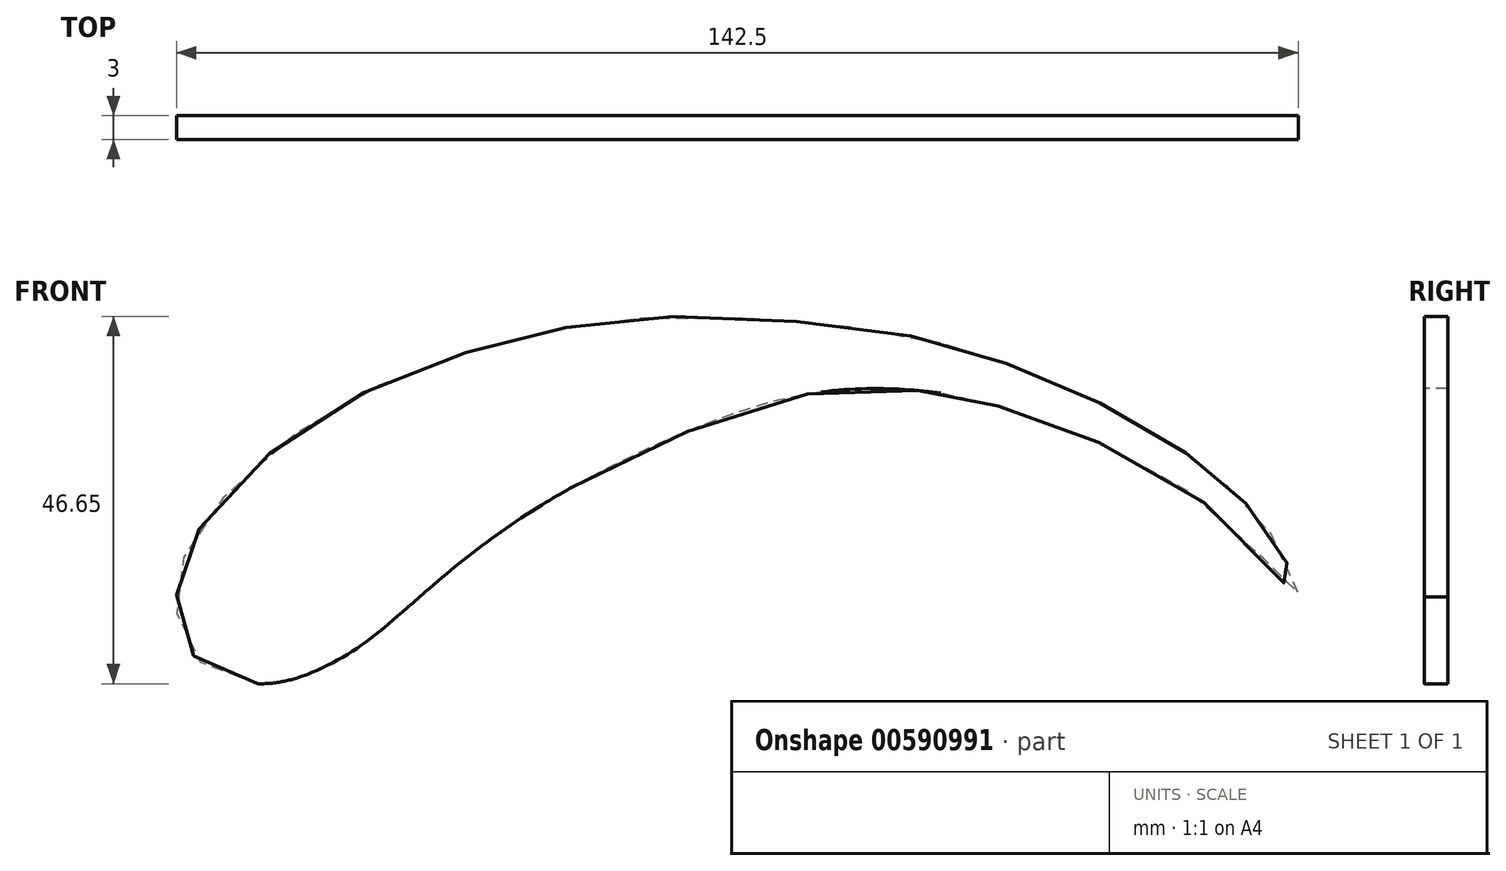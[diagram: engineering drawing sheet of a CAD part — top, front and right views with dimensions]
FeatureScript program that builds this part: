
annotation { "Feature Type Name" : "Feature", "Feature Type Description" : "" }
export const myFeature = defineFeature(function(context is Context, id is Id, definition is map)
    precondition{}
    {
        {
            var Q0;
            Q0=qCreatedBy(makeId("Front.planeOp"),FACE);
            var sketch = newSketch(context, id + "F0", { "sketchPlane" : qUnion([Q0])});
            skFitSpline(sketch, "E0", {"points": [v(70.77, 8.65) * mm, v(64.93, 15.14) * mm, v(49.3, 26.46) * mm, v(33.38, 32.65) * mm, v(25.04, 34.55) * mm, v(9.61, 34.55) * mm, v(-10.88, 27.85) * mm, v(-29.95, 17.24) * mm, v(-42.33, 7.26) * mm, v(-49.15, 1.83) * mm, v(-56.48, -1.7) * mm, v(-63.05, -2.21) * mm, v(-69.11, 0.76) * mm, v(-71.44, 5.7) * mm, v(-71.33, 11.53) * mm, v(-68.1, 18.3) * mm, v(-56.75, 29.26) * mm, v(-41.91, 37.2) * mm, v(-27.15, 41.76) * mm, v(-12.91, 44.04) * mm, v(7.32, 43.62) * mm, v(24.64, 41.1) * mm, v(36.92, 37.07) * mm, v(50.06, 30.99) * mm, v(59.9, 24.38) * mm, v(65.08, 19.5) * mm, v(69.06, 13.64) * mm, v(70.77, 8.65) * mm]});
            skFitSpline(sketch, "E1", {"points": [v(9.58, 31.44) * mm, v(18.14, 32.26) * mm, v(27.38, 31.44) * mm, v(35.86, 29.26) * mm, v(43.38, 26.4) * mm, v(52.16, 21.6) * mm, v(58.85, 16.94) * mm, v(64.56, 12.2) * mm, v(68.46, 7.93) * mm, v(71.09, 3.65) * mm, v(71.77, 1.02) * mm, v(71.09, -1.16) * mm, v(68.69, -2.14) * mm, v(62.6, -0.76) * mm, v(57.42, 3.2) * mm, v(51.56, 8.38) * mm, v(45.1, 13.56) * mm, v(39.1, 17.7) * mm, v(24.07, 25.43) * mm, v(17.54, 28.2) * mm, v(9.58, 31.44) * mm]});
            skLineSegment(sketch, "E2", {"start": v(66.89, -2.05) * mm, "end": v(10.22, -39.5) * mm});
            skLineSegment(sketch, "E3", {"start": v(51.56, 8.38) * mm, "end": v(10.69, -38.59) * mm});
            skLineSegment(sketch, "E4", {"start": v(34.76, 20.06) * mm, "end": v(10.27, -38.38) * mm});
            skLineSegment(sketch, "E5", {"start": v(31.46, 21.76) * mm, "end": v(9.66, -38.89) * mm});
            skLineSegment(sketch, "E6", {"start": v(-61.43, -2.4) * mm, "end": v(-5.4, -43) * mm});
            skLineSegment(sketch, "E7", {"start": v(-42.33, 7.26) * mm, "end": v(-5.83, -42) * mm});
            skLineSegment(sketch, "E8", {"start": v(-25.2, 20.33) * mm, "end": v(-5.5, -41.7) * mm});
            skLineSegment(sketch, "E9", {"start": v(-4.57, -42.69) * mm, "end": v(-21.5, 22.5) * mm});
            skFitSpline(sketch, "E10", {"points": [v(9.36, -38.69) * mm, v(10.71, -40.4) * mm, v(10.74, -41.03) * mm, v(11.25, -41.53) * mm, v(11.81, -42.49) * mm, v(12.61, -43.77) * mm, v(13.3, -45.05) * mm, v(13.51, -46.38) * mm, v(13.25, -47.6) * mm, v(12.45, -48.82) * mm, v(11.28, -49.99) * mm, v(9.21, -51.2) * mm], "startDerivative": vector(11.94, -5.42) * mm, "endDerivative": vector(-19.54, -10.25) * mm});
            skFitSpline(sketch, "E11", {"points": [v(11.28, -48.82) * mm, v(11.5, -50.51) * mm, v(11.98, -51.57) * mm, v(12.45, -53.06) * mm, v(12.8, -54.12) * mm, v(12.88, -55.58) * mm, v(12.8, -57.2) * mm, v(12.45, -57.74) * mm, v(11.58, -58.39) * mm, v(10.73, -58.9) * mm, v(10.26, -59.9) * mm, v(9.57, -60.62) * mm, v(8.07, -61.16) * mm, v(6.44, -61.34) * mm, v(4.79, -61.05) * mm, v(3.43, -60.64) * mm], "startDerivative": vector(1.43, -24.03) * mm, "endDerivative": vector(-14.91, 8.03) * mm});
            skFitSpline(sketch, "E12", {"points": [v(4.79, -60.21) * mm, v(4.54, -61.27) * mm, v(4.05, -61.76) * mm, v(3.77, -62.08) * mm, v(3.66, -62.8) * mm, v(3.6, -63.9) * mm, v(2.62, -64.04) * mm, v(1.13, -63.06) * mm, v(0.2, -62.26) * mm, v(0, -61.44) * mm, v(0, -61.05) * mm, v(0.6, -61.05) * mm, v(1.96, -61.73) * mm, v(2.3, -61.6) * mm, v(2.7, -60.48) * mm, v(2.09, -59.53) * mm, v(1.3, -59.42) * mm, v(0.52, -58.73) * mm, v(-0.22, -58.63) * mm, v(-0.86, -59.05) * mm, v(-0.83, -60.2) * mm, v(-1.12, -61.41) * mm, v(-1.68, -62.34) * mm, v(-2.27, -63.2) * mm, v(-2.27, -64.5) * mm, v(-2.8, -64.9) * mm, v(-3.62, -64.68) * mm, v(-5.3, -63.38) * mm, v(-6.12, -62.29) * mm, v(-6.12, -61.65) * mm, v(-5.13, -61.86) * mm, v(-4.07, -61.81) * mm, v(-3.67, -61.05) * mm, v(-3, -59.16) * mm, v(-2.48, -56.74) * mm, v(-2.21, -55.55) * mm, v(-0.73, -54.75) * mm, v(0.66, -55.55) * mm, v(1.85, -56.05) * mm, v(2, -55.84) * mm, v(2.22, -55.33) * mm, v(1.96, -53.69) * mm, v(1.72, -52.84) * mm, v(1, -52.46) * mm, v(0.36, -52.15) * mm, v(-1.2, -51.96) * mm, v(-2.5, -51.88) * mm, v(-2.9, -51.48) * mm, v(-3.27, -49.62) * mm, v(-3.93, -47.6) * mm, v(-4.1, -46.18) * mm, v(-4.7, -45.51) * mm, v(-5.3, -45) * mm, v(-5.48, -43.11) * mm, v(-4.03, -42.67) * mm, v(-3.4, -42.92) * mm, v(-2.86, -44.28) * mm, v(-2.86, -44.82) * mm, v(-2.48, -45.77) * mm, v(-2.16, -46.93) * mm, v(-1.47, -48.17) * mm, v(-1.28, -49.11) * mm, v(-0.93, -49.08) * mm, v(0, -48.82) * mm, v(1.47, -48.82) * mm, v(2.73, -48.42) * mm, v(2.98, -48.39) * mm, v(2.67, -48.13) * mm, v(2.41, -46.97) * mm, v(2.6, -45.86) * mm, v(3.49, -44.76) * mm, v(4.79, -44.38) * mm, v(5.54, -44.47) * mm, v(6.42, -44.95) * mm, v(6.87, -45.48) * mm, v(7.34, -46.3) * mm, v(7.43, -47.6) * mm, v(7.3, -47.85) * mm, v(8.38, -47.6) * mm, v(10.3, -46.93) * mm, v(10.94, -45.39) * mm, v(10.88, -44.16) * mm, v(10.3, -43.05) * mm, v(9.83, -41.79) * mm, v(9.7, -41.44) * mm, v(9.08, -41.19) * mm, v(8.29, -40.5) * mm, v(8.32, -39.32) * mm, v(9.36, -38.69) * mm], "startDerivative": vector(-11.38, -101.96) * mm, "endDerivative": vector(113.94, 25.27) * mm});
            skLineSegment(sketch, "E13.trimOffspring", {"start": v(10.69, -38.59) * mm, "end": v(62.6, -0.76) * mm});
            skLineSegment(sketch, "E14.trimOffspring", {"start": v(10.27, -38.38) * mm, "end": v(49.05, 10.44) * mm});
            skLineSegment(sketch, "E15.trimOffspring", {"start": v(-5.5, -41.7) * mm, "end": v(-38.93, 10.2) * mm});
            skLineSegment(sketch, "E16.trimOffspring", {"start": v(-5.83, -42) * mm, "end": v(-56.48, -1.7) * mm});
            skSolve(sketch);
        }
        {
            var Q0;
            Q0=makeQuery(id+"F0.imprint","IMPRINT",FACE,{"disambiguationData":[TD([[makeQuery(id+"F0.imprint","IMPRINT",EDGE,{"derivedFrom":sQuery(id+"F0.wireOp",EDGE,"E0")}),-1.0]])]});
            extrude(context, id + "F1", {"entities" : qUnion([Q0]), "depth" : 3 * mm, "offsetDistance" : 25 * mm});
        }
    });
